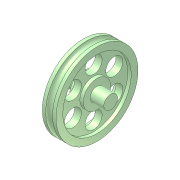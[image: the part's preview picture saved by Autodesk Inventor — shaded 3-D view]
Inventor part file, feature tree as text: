
AUTODESK INVENTOR PART (.ipt)
format: ipt  version: unknown  size: 247,296 bytes
history: native  units: in
note: dims shown in document units (in); Inventor stores cm internally (conversion verified against a paired STEP export)
features: sketch x3, revolve x2, extrude x1, pattern_circular x1
ambient origin geometry x8: Origin, YZ Plane, XZ Plane, XY Plane, X Axis, Y Axis, Z Axis, Center Point
feature tree (7):
  revolve  "Revolution1"  [1 undecoded]
  extrude  "Extrusion3"  Depth=0.0394in
  pattern_circular  "Circular Pattern3"  [2 undecoded]
  revolve  "Revolution2"  [1 undecoded]
  sketch  "Sketch1"  dims[d0=0.2362in d1=0.0394in]
  sketch  "Sketch4"  dims[d2=0.2756in d3=0.0394in d4=0.0394in]
  sketch  "Sketch5"  dims[d5=90.0deg d24=0.0394in d25=0.0394in d34=0.0197in d35=0.0394in d39=0.1378in d40=0.0984in d41=0.3937in d42=0.0in d43=2.3622in d44=360.0deg d46=0.0in d47=0.0787in d48=0.0787in d49=0.0394in d50=90.0deg]
note: 4 required parameter values undecoded (feature->parameter linkage not recoverable at this tier; creation-order binding heuristic only, values carry confidence <= 0.55)